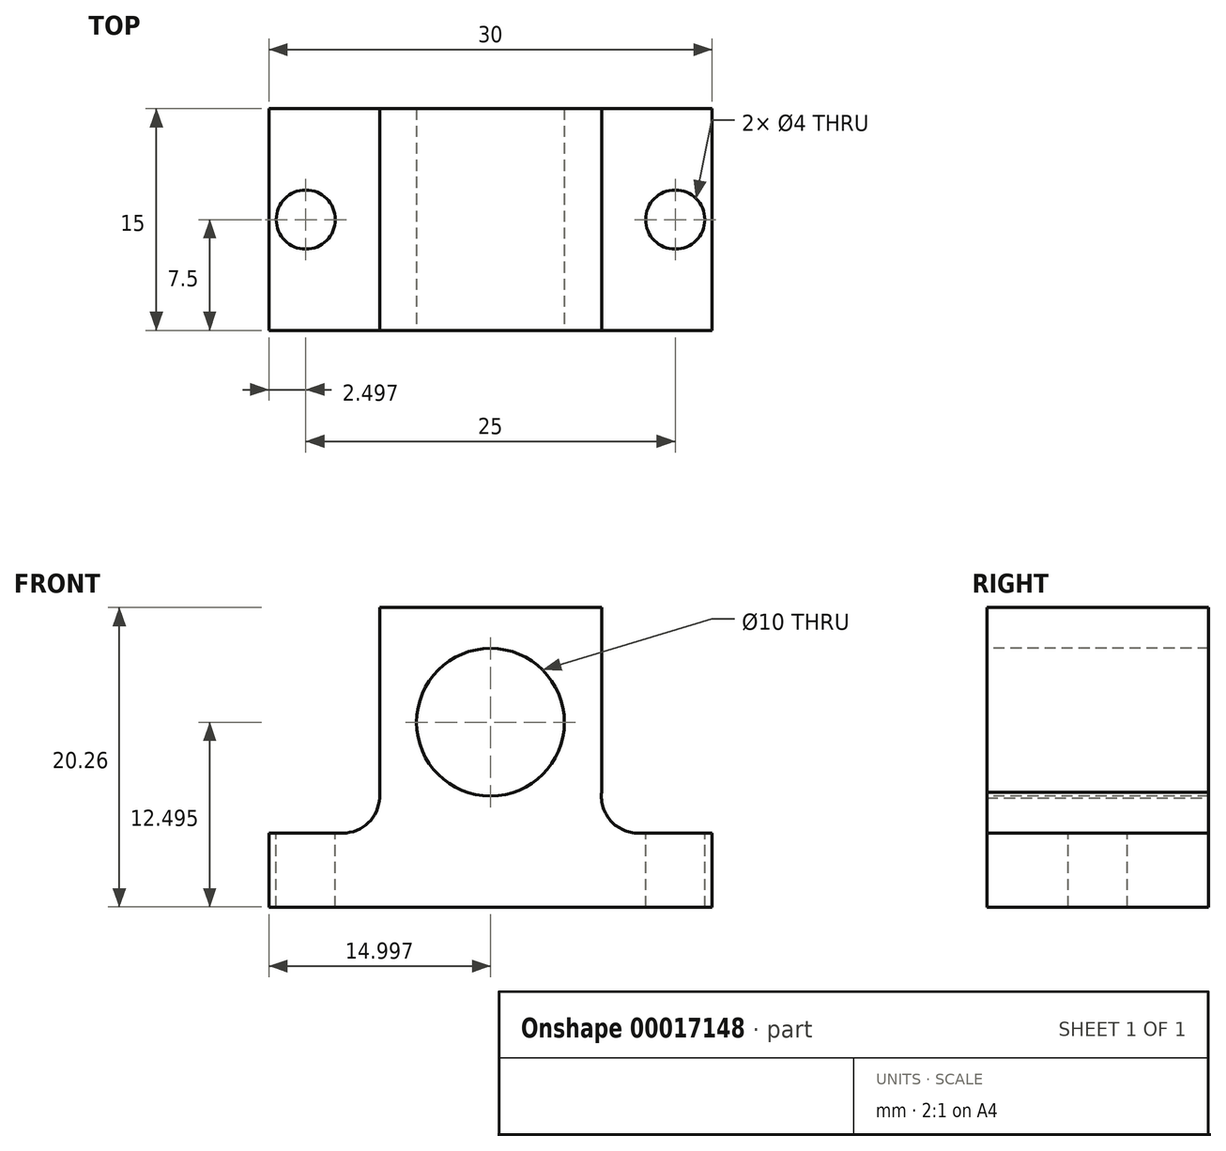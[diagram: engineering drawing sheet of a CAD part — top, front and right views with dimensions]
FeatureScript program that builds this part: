
annotation { "Feature Type Name" : "Feature", "Feature Type Description" : "" }
export const myFeature = defineFeature(function(context is Context, id is Id, definition is map)
    precondition{}
    {
        {
            var Q0;
            Q0=qCreatedBy(makeId("Front.planeOp"),FACE);
            var sketch = newSketch(context, id + "F0", { "sketchPlane" : qUnion([Q0])});
            skLineSegment(sketch, "E0", {"start": v(-13.8, -24.71) * mm, "end": v(16.2, -24.71) * mm});
            skLineSegment(sketch, "E1", {"start": v(16.2, -24.71) * mm, "end": v(16.2, -19.71) * mm});
            skLineSegment(sketch, "E2", {"start": v(16.2, -19.71) * mm, "end": v(11.2, -19.71) * mm});
            skLineSegment(sketch, "E3", {"start": v(-13.8, -24.71) * mm, "end": v(-13.8, -19.71) * mm});
            skLineSegment(sketch, "E4", {"start": v(-13.8, -19.71) * mm, "end": v(-8.8, -19.71) * mm});
            skArc(sketch, "E5", {"start": v(11.2, -19.71) * mm, "mid": v(9.34, -18.89) * mm, "end": v(8.71, -16.95) * mm});
            skArc(sketch, "E6", {"start": v(-8.8, -19.71) * mm, "mid": v(-7.07, -19.02) * mm, "end": v(-6.3, -17.32) * mm});
            skLineSegment(sketch, "E7.top", {"start": v(-6.3, -4.45) * mm, "end": v(8.71, -4.45) * mm});
            skLineSegment(sketch, "E7.left", {"start": v(-6.3, -17.32) * mm, "end": v(-6.3, -4.45) * mm});
            skLineSegment(sketch, "E7.right", {"start": v(8.71, -16.95) * mm, "end": v(8.71, -4.45) * mm});
            skSolve(sketch);
        }
        {
            var Q0;
            Q0 = qSketchRegion(id + "F0", true);
            extrude(context, id + "F1", {"entities" : qUnion([Q0]), "depth" : 15 * mm});
        }
        {
            var Q0;
            Q0=makeQuery(id+"F1.opExtrude","CAP_FACE",FACE,{"disambiguationData":[OSD([sQuery(id+"F0.wireOp",EDGE,"E0"),sQuery(id+"F0.wireOp",EDGE,"E1"),sQuery(id+"F0.wireOp",EDGE,"E2"),sQuery(id+"F0.wireOp",EDGE,"E3"),sQuery(id+"F0.wireOp",EDGE,"E4"),sQuery(id+"F0.wireOp",EDGE,"E5"),sQuery(id+"F0.wireOp",EDGE,"E6"),sQuery(id+"F0.wireOp",EDGE,"E7.top"),sQuery(id+"F0.wireOp",EDGE,"E7.left"),sQuery(id+"F0.wireOp",EDGE,"E7.right")])],"isStart":false});
            var sketch = newSketch(context, id + "F2", { "sketchPlane" : qUnion([Q0])});
            skCircle(sketch, "E8", {"center": v(1.2, -12.21) * mm, "radius": 5 * mm});
            skSolve(sketch);
        }
        {
            var Q0;
            Q0=makeQuery(id+"F2.imprint","IMPRINT",FACE,{"disambiguationData":[TD([[makeQuery(id+"F2.imprint","IMPRINT",EDGE,{"derivedFrom":sQuery(id+"F2.wireOp",EDGE,"E8")}),1.0]])]});
            extrude(context, id + "F3", {"entities" : qUnion([Q0]), "operationType" : NewBodyOperationType.REMOVE, "endBound" : BoundingType.THROUGH_ALL, "oppositeDirection" : true, "depth" : 25 * mm});
        }
        {
            var Q0;
            Q0=makeQuery(id+"F1.opExtrude","SWEPT_FACE",FACE,{"disambiguationData":[OSD([sQuery(id+"F0.wireOp",EDGE,"E4")])]});
            var sketch = newSketch(context, id + "F4", { "sketchPlane" : qUnion([Q0])});
            skCircle(sketch, "E9", {"center": v(-11.3, -7.5) * mm, "radius": 2 * mm});
            skSolve(sketch);
        }
        {
            var Q0;
            Q0=makeQuery(id+"F1.opExtrude","SWEPT_FACE",FACE,{"disambiguationData":[OSD([sQuery(id+"F0.wireOp",EDGE,"E2")])]});
            var sketch = newSketch(context, id + "F5", { "sketchPlane" : qUnion([Q0])});
            skCircle(sketch, "E10", {"center": v(13.7, -7.5) * mm, "radius": 2 * mm});
            skSolve(sketch);
        }
        {
            var Q0;
            Q0=makeQuery(id+"F4.imprint","IMPRINT",FACE,{"disambiguationData":[TD([[makeQuery(id+"F4.imprint","IMPRINT",EDGE,{"derivedFrom":sQuery(id+"F4.wireOp",EDGE,"E9")}),1.0]])]});
            var Q1;
            Q1=makeQuery(id+"F5.imprint","IMPRINT",FACE,{"disambiguationData":[TD([[makeQuery(id+"F5.imprint","IMPRINT",EDGE,{"derivedFrom":sQuery(id+"F5.wireOp",EDGE,"E10")}),1.0]])]});
            extrude(context, id + "F6", {"entities" : qUnion([Q0, Q1]), "operationType" : NewBodyOperationType.REMOVE, "endBound" : BoundingType.THROUGH_ALL, "oppositeDirection" : true, "depth" : 25 * mm});
        }
    });
